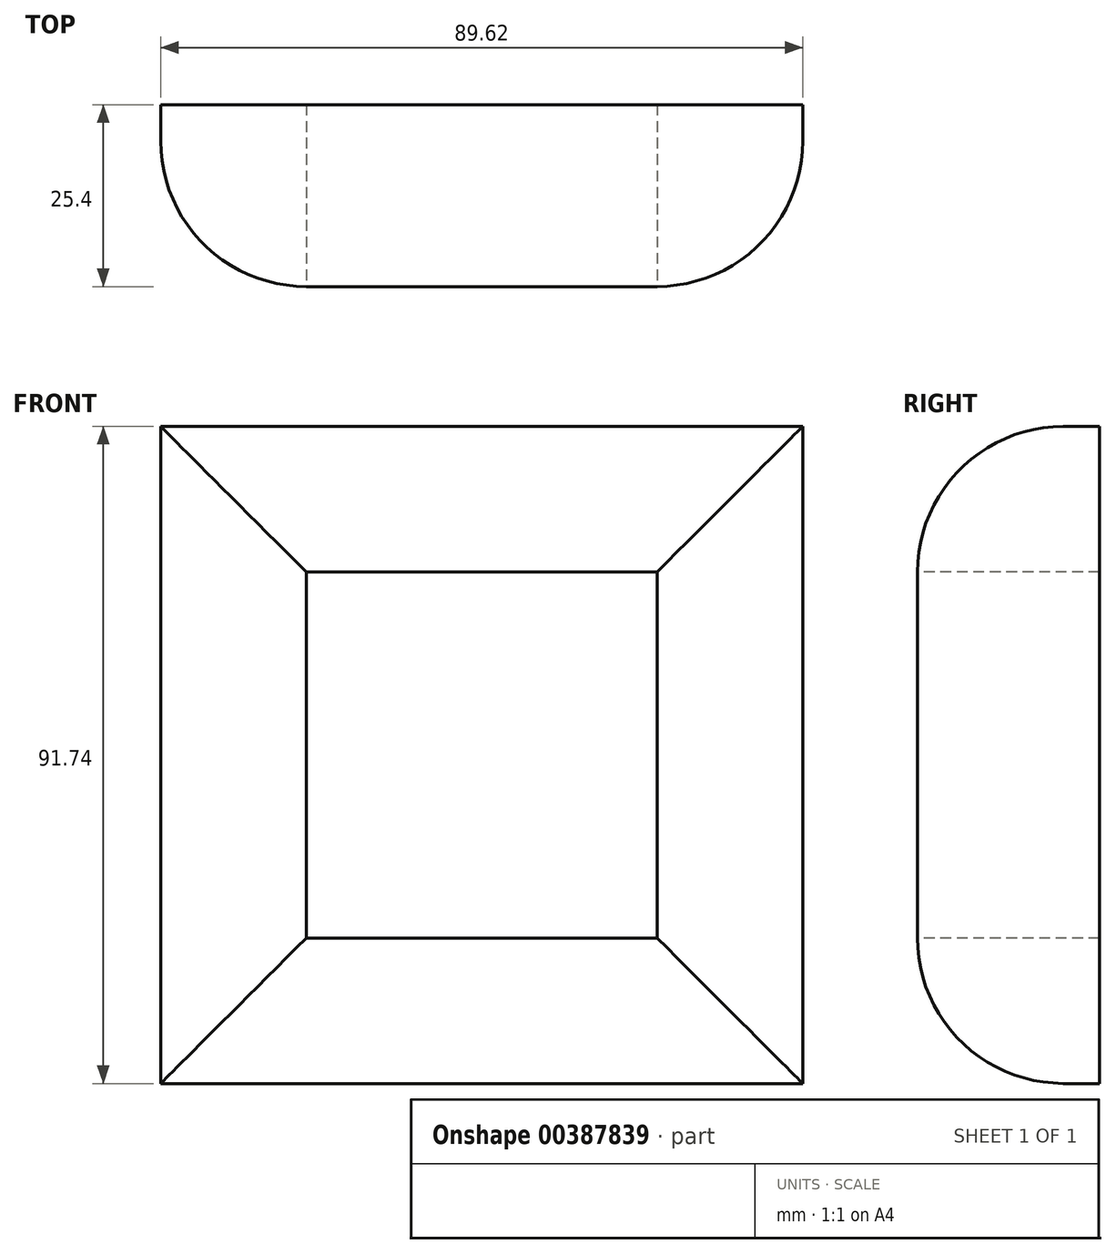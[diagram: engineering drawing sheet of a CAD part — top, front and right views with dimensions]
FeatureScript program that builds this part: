
annotation { "Feature Type Name" : "Feature", "Feature Type Description" : "" }
export const myFeature = defineFeature(function(context is Context, id is Id, definition is map)
    precondition{}
    {
        {
            var Q0;
            Q0=qCreatedBy(makeId("Front.planeOp"),FACE);
            var sketch = newSketch(context, id + "F0", { "sketchPlane" : qUnion([Q0])});
            skLineSegment(sketch, "E0.bottom", {"start": v(44.8, -45.87) * mm, "end": v(-44.8, -45.87) * mm});
            skLineSegment(sketch, "E0.top", {"start": v(44.8, 45.87) * mm, "end": v(-44.8, 45.87) * mm});
            skLineSegment(sketch, "E0.left", {"start": v(44.8, -45.87) * mm, "end": v(44.8, 45.87) * mm});
            skLineSegment(sketch, "E0.right", {"start": v(-44.8, -45.87) * mm, "end": v(-44.8, 45.87) * mm});
            skPoint(sketch, "E0.middle", {"position": v(0, 0) * mm});
            skSolve(sketch);
        }
        {
            var Q0;
            Q0=makeQuery(id+"F0.imprint","IMPRINT",FACE,{"disambiguationData":[TD([[makeQuery(id+"F0.imprint","IMPRINT",EDGE,{"derivedFrom":sQuery(id+"F0.wireOp",EDGE,"E0.bottom")}),-1.0]])]});
            extrude(context, id + "F1", {"entities" : qUnion([Q0]), "depth" : 25.4 * mm});
        }
        {
            var Q0;
            Q0=makeQuery(id+"F1.opExtrude","CAP_EDGE",EDGE,{"disambiguationData":[OSD([sQuery(id+"F0.wireOp",EDGE,"E0.left")])],"isStart":false});
            var Q1;
            Q1=makeQuery(id+"F1.opExtrude","CAP_EDGE",EDGE,{"disambiguationData":[OSD([sQuery(id+"F0.wireOp",EDGE,"E0.top")])],"isStart":false});
            var Q2;
            Q2=makeQuery(id+"F1.opExtrude","CAP_EDGE",EDGE,{"disambiguationData":[OSD([sQuery(id+"F0.wireOp",EDGE,"E0.right")])],"isStart":false});
            var Q3;
            Q3=makeQuery(id+"F1.opExtrude","CAP_EDGE",EDGE,{"disambiguationData":[OSD([sQuery(id+"F0.wireOp",EDGE,"E0.bottom")])],"isStart":false});
            fillet(context, id + "F2", {"entities" : qUnion([Q0, Q1, Q2, Q3]), "radius" : 20.32 * mm, "tangentPropagation" : true, "allowEdgeOverflow" : false});
        }
        {
            var Q0;
            Q0=qCreatedBy(makeId("Front.planeOp"),FACE);
            var sketch = newSketch(context, id + "F3", { "sketchPlane" : qUnion([Q0])});
            skLineSegment(sketch, "E1.bottom", {"start": v(24.69, -25.45) * mm, "end": v(-24.69, -25.45) * mm});
            skLineSegment(sketch, "E1.top", {"start": v(24.69, 25.45) * mm, "end": v(-24.69, 25.45) * mm});
            skLineSegment(sketch, "E1.left", {"start": v(24.69, -25.45) * mm, "end": v(24.69, 25.45) * mm});
            skLineSegment(sketch, "E1.right", {"start": v(-24.69, -25.45) * mm, "end": v(-24.69, 25.45) * mm});
            skPoint(sketch, "E1.middle", {"position": v(0, 0) * mm});
            skSolve(sketch);
        }
        {
            var Q0;
            Q0 = qSketchRegion(id + "F3", true);
            var Q1;
            Q1=makeQuery(id+"F1.opExtrude","CAP_FACE",FACE,{"disambiguationData":[OSD([sQuery(id+"F0.wireOp",EDGE,"E0.bottom"),sQuery(id+"F0.wireOp",EDGE,"E0.top"),sQuery(id+"F0.wireOp",EDGE,"E0.left"),sQuery(id+"F0.wireOp",EDGE,"E0.right")])],"isStart":false});
            extrude(context, id + "F4", {"entities" : qUnion([Q0, Q1]), "operationType" : NewBodyOperationType.REMOVE, "oppositeDirection" : true, "depth" : 127 * mm});
        }
    });
